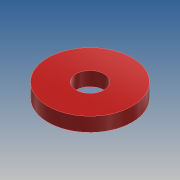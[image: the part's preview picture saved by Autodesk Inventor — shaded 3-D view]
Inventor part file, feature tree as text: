
AUTODESK INVENTOR PART (.ipt)
format: ipt  version: 2017 (Build 210142000, 142)  size: 84,480 bytes
history: native  units: mm
features: other x1, extrude x1, sketch x1
ambient origin geometry x8: Origin, YZ Plane, XZ Plane, XY Plane, X Axis, Y Axis, Z Axis, Center Point
bodies: Body1 (feature_tree)
feature tree (3):
  other  "Sólido1"
  extrude  "Extrusión1"  Depth=2.0mm
  sketch  "Boceto1"  dims[d0=4.0mm d1=12.0mm d2=2.0mm d3=0.0mm]
